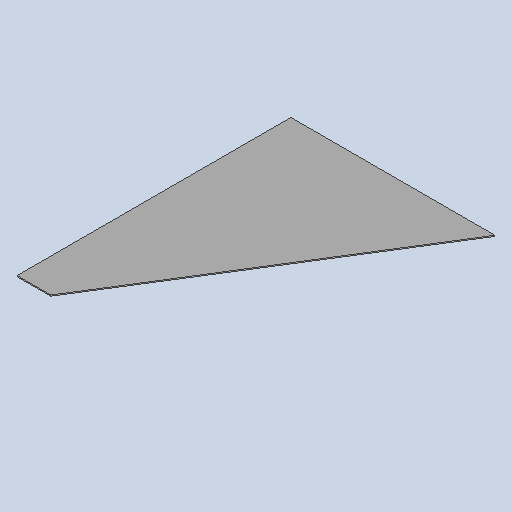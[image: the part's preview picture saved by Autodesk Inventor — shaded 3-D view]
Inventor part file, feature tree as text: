
AUTODESK INVENTOR PART (.ipt)
format: ipt  version: 2025 (Build 290162010, 162A)  size: 103,936 bytes
history: native  units: mm
features: other x2, sheet_metal_op x1, sketch x1
ambient origin geometry x8: Origin, YZ Plane, XZ Plane, XY Plane, X Axis, Y Axis, Z Axis, Center Point
bodies: Body1 (feature_tree)
feature tree (4):
  sheet_metal_op  "Face2"
  sketch  "Sketch5"  dims[d28=3.0mm d37=100.0mm d38=812.0mm d39=605.0mm]
  other  "Plate4"
  other  "Definition1"
